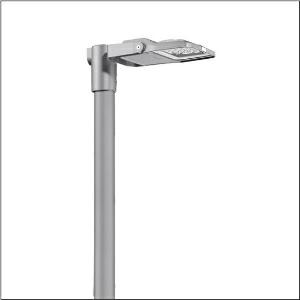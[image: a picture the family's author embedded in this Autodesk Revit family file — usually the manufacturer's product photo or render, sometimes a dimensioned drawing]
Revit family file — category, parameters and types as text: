
# Revit family: floodlight_fl_21_iq_micro___pl43_5xa7761a2a3a_2bb2
name_source: partatom
category: Lighting Fixtures
units: mm (PartAtom-declared; Revit-internal decimal feet)

## family parameters
Cut with Voids When Loaded = No
Host = Face
Light Source = No
Part Type = Normal
Room Calculation Point = No
Round Connector Dimension = Use Diameter
Shared = No

## types (1)
- --- (1 x LED, 3040 lm, 23.1 W, 3000K)
    Apparent Load = 23 VA
    CIE Flux Codes = 29 80 99 100 100
    Color Rendering = 70
    Color Temperature = 3000K
    Default Elevation = 1800 mm
    Description = Floodlight FL 21 iQ micro, floodlight, primary light control with lens, of PMMA, primary optical cover: protective disc, of toughened safety glass, transparent, light distribution: PL43, light emission: direct distribution, installation type: surface-mounted, LED, High Power LED, rated luminous flux: 3.040lm, luminous efficacy: 132lm/W, light colour: 730, colour temperature: 3000K, control: optimised constant luminous flux control (CLO 2.0), Desk-Remote (wireless, voltage-free reading and setting of iQ features in the workshop via application-optimized NFC function/RFID function), Light-Fading, Smart-Wire, Night-Set, Lumen-Switch, Temp-Guard, Auto-Match, with terminal, 6-pole, mains connection: 220..240V, AC, 50/60Hz, start of lifetime: 23W, end of service life: 24W, reduction: 11W, luminaire housing, of diecast aluminium, powder-coated, Siteco® metallic grey (DB 702S), corrosivity category C5 mid according to DIN EN ISO 12944, sealing non-destructively replaceable, please order mast flange separately, mast bracket, of steel, galvanised, powder-coated, Siteco® metallic grey (DB 702S), protection rating (complete): IP66, insulation class (complete): insulation class II (safety insulation), certification: CE, ENEC, VDE, protection symbol: D, impact resistance: IK07, permissible operating ambient temperature: -40..+40°C, permissible operating ambient temperature for outdoor applications: -40..+50°C, standard: DIN EN 12944, LABS conformity tested according to VDMA 24364:2018-05, packaging unit: 1 piece

Light Distribution: PL43
    Height = 65 mm
    Lamp = 1 x LED
    Lamp Light Flux = 3040 lm
    Lamp Power = 23.1 W
    Lamp count = 1
    Length = 312 mm
    Luminous efficacy = 132 lm/W
    Manufacturer = Siteco
    ModVariant = No
    Model = 5XA7761A2A3A
    Number of Poles = 1
    OnlyDefault = Yes
    Power Factor = 1
    Product Name = Floodlight FL 21 iQ micro | PL43
    Product group = floodlight | pylon top
    ProductGroupID = 6101
    Protection Class = Protection class II
    Protection Degree = IP 66
    RLX_Detail_Level = 1
    RLX_Emergency_Light_Flux = 0 lm
    RLX_Emergency_Type = 0
    RLX_Emergency_Type_DB = No
    RlxData = <blob elided: 101745 chars, md5=39a0ddc1>
    Socket = socket
    Standby Power = 0 W
    System Light Flux = 3040 lm
    System Power = 23 W
    Type Comments = factory setting: luminous flux: 100 % | dim-lin: 254 | 455 mA
    Type Image = l_1007121.jpg
    URL = http://relux.com
    VarID = @adj_127991
    Voltage = 0 V
    Weight = 0.00 kg
    Width = 230 mm

## geometry (parser evidence)
native form markers: Blend x4, Sweep x13
no freeform markers — native parametric forms only
